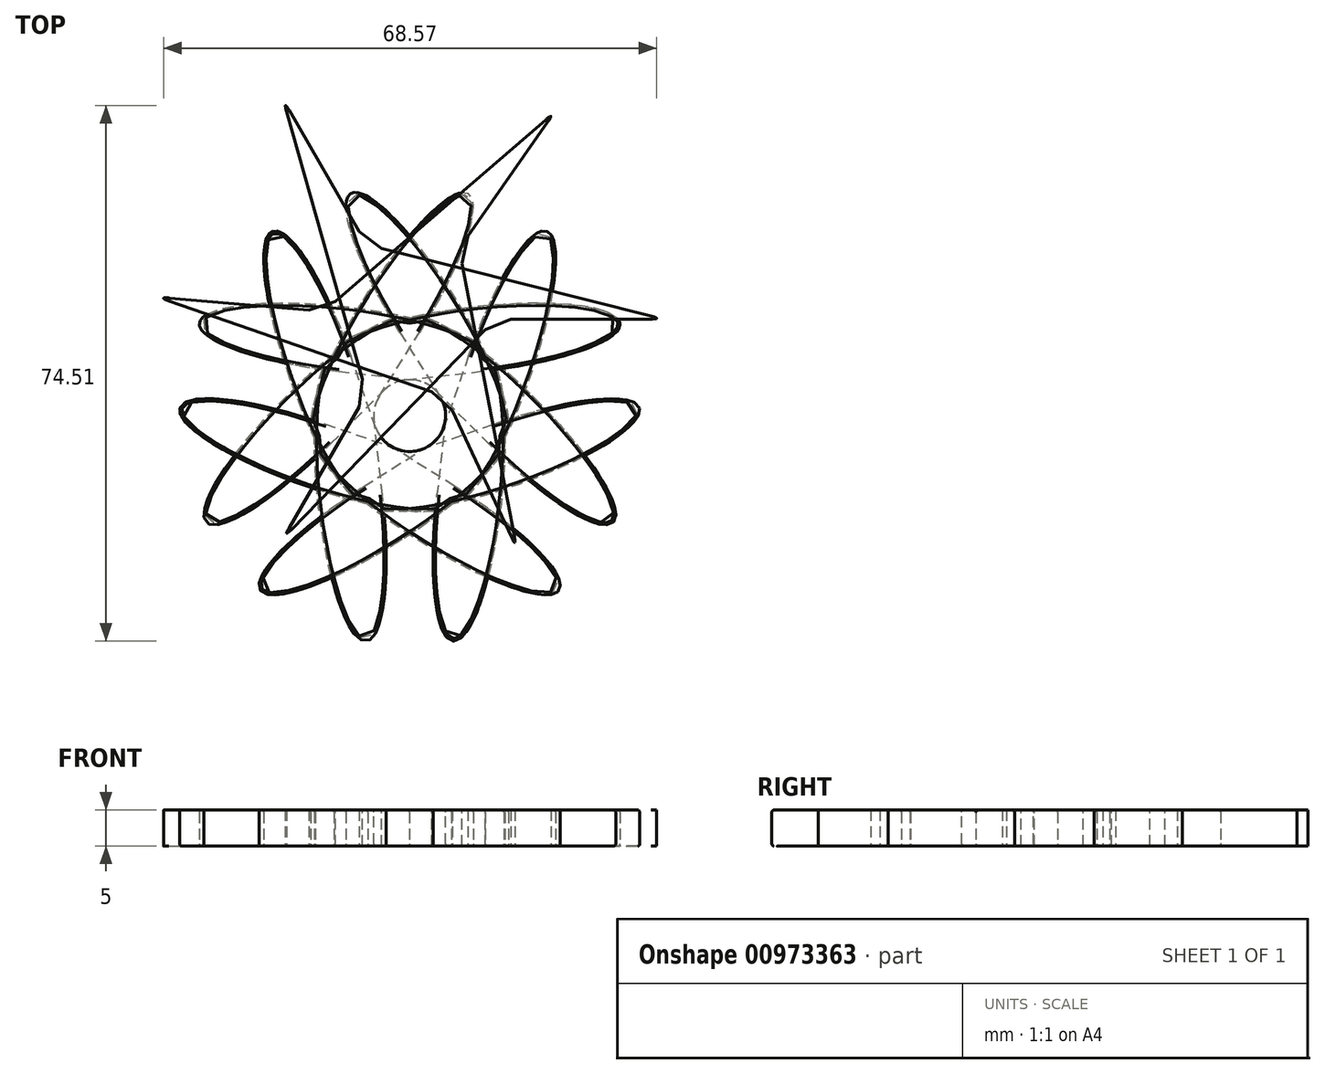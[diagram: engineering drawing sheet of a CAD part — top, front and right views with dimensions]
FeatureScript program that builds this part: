
annotation { "Feature Type Name" : "Feature", "Feature Type Description" : "" }
export const myFeature = defineFeature(function(context is Context, id is Id, definition is map)
    precondition{}
    {
        {
            var Q0;
            Q0=qCreatedBy(makeId("Top.planeOp"),FACE);
            var sketch = newSketch(context, id + "F0", { "sketchPlane" : qUnion([Q0])});
            skLineSegment(sketch, "E0", {"start": v(0, 0) * mm, "end": v(-2.73, 0) * mm});
            skLineSegment(sketch, "E1", {"start": v(0, 0) * mm, "end": v(0, -2.73) * mm});
            skLineSegment(sketch, "E2", {"start": v(0, 0) * mm, "end": v(-28.28, -28.28) * mm});
            skEllipticalArc(sketch, "E3", {});
            skLineSegment(sketch, "E4", {"start": v(0, -15.88) * mm, "end": v(0, 19.12) * mm});
            skEllipticalArc(sketch, "E5.MirrorC", {});
            skLineSegment(sketch, "E6.MirrorCS", {"start": v(0, 0) * mm, "end": v(28.28, -28.28) * mm});
            skLineSegment(sketch, "E7", {"start": v(-10.96, -17.32) * mm, "end": v(0, -6.36) * mm});
            skLineSegment(sketch, "E8", {"start": v(0, -6.36) * mm, "end": v(10.96, -17.32) * mm});
            const initialGuessF0  = {"E3": [-0.014142135623730956, -0.014142135623730956, 0.7071067811865476, 0.7071067811865476, 0.02, 0.0045, 0, 5.840556422484005], "E5.MirrorC": [0.014142135623730956, -0.014142135623730956, -0.7071067811865476, 0.7071067811865476, 0.02, 0.0045, 0.4426288846955803, 0]};
            skSetInitialGuess(sketch, initialGuessF0);
            skSolve(sketch);
        }
        {
            var Q0;
            {var subQ0=sQuery(id+"F0.wireOp",EDGE,"E1");var subQ1=makeQuery(id+"F0.imprint","IMPRINT",EDGE,{"derivedFrom":subQ0});var subQ2=sQuery(id+"F0.wireOp",EDGE,"E6.MirrorCS");var subQ3=makeQuery(id+"F0.imprint","IMPRINT",EDGE,{"derivedFrom":subQ2});var subQ8=sQuery(id+"F0.wireOp",EDGE,"E8");var subQ12=sQuery(id+"F0.wireOp",EDGE,"E7");var subQ19=sQuery(id+"F0.wireOp",EDGE,"E0");var subQ20=makeQuery(id+"F0.imprint","IMPRINT",EDGE,{"derivedFrom":subQ19});Q0=qUnion([makeQuery(id+"F0.imprint","IMPRINT",FACE,{"disambiguationData":[TD([[subQ20,-1.0]])]}),makeQuery(id+"F0.imprint","IMPRINT",FACE,{"disambiguationData":[TD([[subQ3,1.0]])]}),makeQuery(id+"F0.imprint","IMPRINT",FACE,{"disambiguationData":[TD([[subQ20,1.0]])]}),makeQuery(id+"F0.imprint","IMPRINT",FACE,{"disambiguationData":[TD([[makeQuery(id+"F0.imprint","IMPRINT",EDGE,{"derivedFrom":subQ12}),1.0]])]}),makeQuery(id+"F0.imprint","IMPRINT",FACE,{"disambiguationData":[TD([[makeQuery(id+"F0.imprint","IMPRINT",EDGE,{"derivedFrom":subQ8}),1.0]])]}),makeQuery(id+"F0.imprint","IMPRINT",FACE,{"disambiguationData":[TD([[subQ1,-1.0]])]}),makeQuery(id+"F0.imprint","IMPRINT",FACE,{"disambiguationData":[TD([[subQ1,1.0]])]})]);}
            extrude(context, id + "F1", {"entities" : qUnion([Q0]), "depth" : 5 * mm, "offsetDistance" : 25 * mm});
        }
        {
            var Q0;
            Q0=makeQuery(id+"F1.opExtrude","SWEPT_EDGE",EDGE,{"disambiguationData":[OSD([sQuery(id+"F0.wireOp",EDGE,"E4"),sQuery(id+"F0.wireOp",EDGE,"E7"),sQuery(id+"F0.wireOp",EDGE,"E8")])]});
            fillet(context, id + "F2", {"entities" : qUnion([Q0]), "tangentPropagation" : true, "radius" : 5 * mm, "defaultsChanged" : false, "vertexSettings" : [], "allowEdgeOverflow" : false});
        }
        {
            var Q0;
            Q0=makeQuery(id+"F1.opExtrude","CAP_FACE",FACE,{"disambiguationData":[OSD([sQuery(id+"F0.wireOp",EDGE,"E3"),sQuery(id+"F0.wireOp",EDGE,"E5.MirrorC"),sQuery(id+"F0.wireOp",EDGE,"E7"),sQuery(id+"F0.wireOp",EDGE,"E8")])],"isStart":false});
            var Q1;
            Q1=makeQuery(id+"F1.opExtrude","CAP_FACE",FACE,{"disambiguationData":[OSD([sQuery(id+"F0.wireOp",EDGE,"E3"),sQuery(id+"F0.wireOp",EDGE,"E5.MirrorC"),sQuery(id+"F0.wireOp",EDGE,"E7"),sQuery(id+"F0.wireOp",EDGE,"E8")])],"isStart":true});
            fillet(context, id + "F3", {"entities" : qUnion([Q0, Q1]), "tangentPropagation" : true, "radius" : 0.3 * mm, "defaultsChanged" : true, "vertexSettings" : [], "allowEdgeOverflow" : false});
        }
        {
            var Q0;
            Q0=makeQuery(id+"F1.opExtrude","SWEPT_BODY",BODY,{"disambiguationData":[OSD([sQuery(id+"F0.wireOp",EDGE,"E3"),sQuery(id+"F0.wireOp",EDGE,"E5.MirrorC"),sQuery(id+"F0.wireOp",EDGE,"E7"),sQuery(id+"F0.wireOp",EDGE,"E8")])]});
            var Q1;
            {var subQ0=sQuery(id+"F0.wireOp",EDGE,"E8");var subQ1=sQuery(id+"F0.wireOp",EDGE,"E7");var subQ2=makeQuery(id+"F1.opExtrude","CAP_FACE",FACE,{"disambiguationData":[OSD([sQuery(id+"F0.wireOp",EDGE,"E3"),sQuery(id+"F0.wireOp",EDGE,"E5.MirrorC"),subQ1,subQ0])],"isStart":true});Q1=makeQuery(id+"F3.opFillet","BLEND_EDGE",EDGE,{"blendedFrom":[makeQuery(id+"F2.opFillet","BLEND_EDGE",EDGE,{"blendedFrom":[makeQuery(id+"F1.opExtrude","SWEPT_EDGE",EDGE,{"disambiguationData":[OSD([sQuery(id+"F0.wireOp",EDGE,"E4"),subQ1,subQ0])]}),subQ2],"blendedInto":[subQ2]}),subQ2],"blendedInto":[subQ2]});}
            circularPattern(context, id + "F4", {"entities" : qUnion([Q0]), "axis" : qUnion([Q1]), "angle" : 360 * degree, "instanceCount" : 7, "equalSpace" : true});
        }
        {
            var Q0;
            Q0=qCreatedBy(makeId("Top.planeOp"),FACE);
            var sketch = newSketch(context, id + "F5", { "sketchPlane" : qUnion([Q0])});
            skLineSegment(sketch, "E9", {"start": v(0, 0) * mm, "end": v(0, 1) * mm});
            skLineSegment(sketch, "E10", {"start": v(35.14, 0) * mm, "end": v(0, 0) * mm});
            skLineSegment(sketch, "E11", {"start": v(0, 0) * mm, "end": v(7.07, 7.07) * mm});
            skLineSegment(sketch, "E12", {"start": v(7.07, 7.07) * mm, "end": v(35.14, 0) * mm});
            skCircle(sketch, "E13", {"center": v(0, 0) * mm, "radius": 1 * mm});
            skLineSegment(sketch, "E14.1.0", {"start": v(-9.66, 2.59) * mm, "end": v(-17.57, 30.43) * mm});
            skLineSegment(sketch, "E14.1.2", {"start": v(0, 0) * mm, "end": v(-9.66, 2.59) * mm});
            skLineSegment(sketch, "E14.2.0", {"start": v(2.59, -9.66) * mm, "end": v(-17.57, -30.43) * mm});
            skLineSegment(sketch, "E14.2.2", {"start": v(0, 0) * mm, "end": v(2.59, -9.66) * mm});
            skLineSegment(sketch, "E15", {"start": v(-17.57, 30.43) * mm, "end": v(0, 0) * mm});
            skLineSegment(sketch, "E16", {"start": v(-17.57, -30.43) * mm, "end": v(0, 0) * mm});
            skLineSegment(sketch, "E17", {"start": v(0, 0) * mm, "end": v(35.14, 0) * mm});
            skLineSegment(sketch, "E18", {"start": v(2.59, -9.66) * mm, "end": v(11.96, 0) * mm});
            skLineSegment(sketch, "E19.1.0", {"start": v(-9.66, 2.59) * mm, "end": v(-5.98, -10.36) * mm});
            skLineSegment(sketch, "E19.2.0", {"start": v(7.07, 7.07) * mm, "end": v(-5.98, 10.36) * mm});
            skLineSegment(sketch, "E19.anchor1", {"start": v(0, 0) * mm, "end": v(2.59, -9.66) * mm, "construction": true});
            skLineSegment(sketch, "E19.anchor2", {"start": v(0, 0) * mm, "end": v(7.07, 7.07) * mm, "construction": true});
            skSolve(sketch);
        }
        {
            var Q0;
            {var subQ3=sQuery(id+"F5.wireOp",EDGE,"E12");Q0=makeQuery(id+"F5.imprint","IMPRINT",FACE,{"disambiguationData":[TD([[makeQuery(id+"F5.imprint","IMPRINT",EDGE,{"derivedFrom":subQ3}),-1.0]])]});}
            var Q1;
            {var subQ0=sQuery(id+"F5.wireOp",EDGE,"E19.2.0");Q1=makeQuery(id+"F5.imprint","IMPRINT",FACE,{"disambiguationData":[TD([[makeQuery(id+"F5.imprint","IMPRINT",EDGE,{"derivedFrom":subQ0}),1.0]])]});}
            var Q2;
            {var subQ5=sQuery(id+"F5.wireOp",EDGE,"E19.1.0");Q2=makeQuery(id+"F5.imprint","IMPRINT",FACE,{"disambiguationData":[TD([[makeQuery(id+"F5.imprint","IMPRINT",EDGE,{"derivedFrom":subQ5}),1.0]])]});}
            var Q3;
            {var subQ1=sQuery(id+"F5.wireOp",EDGE,"E14.2.0");Q3=makeQuery(id+"F5.imprint","IMPRINT",FACE,{"disambiguationData":[TD([[makeQuery(id+"F5.imprint","IMPRINT",EDGE,{"derivedFrom":subQ1}),-1.0]])]});}
            var Q4;
            {var subQ0=sQuery(id+"F5.wireOp",EDGE,"E14.1.0");Q4=makeQuery(id+"F5.imprint","IMPRINT",FACE,{"disambiguationData":[TD([[makeQuery(id+"F5.imprint","IMPRINT",EDGE,{"derivedFrom":subQ0}),-1.0]])]});}
            var Q5;
            {var subQ0=sQuery(id+"F5.wireOp",EDGE,"E14.2.2");var subQ3=sQuery(id+"F5.wireOp",EDGE,"E13");var subQ5=makeQuery(id+"F5.imprint","INTERSECT",VERTEX,{"derivedFrom":[subQ3,subQ0]});Q5=makeQuery(id+"F5.imprint","IMPRINT",FACE,{"disambiguationData":[TD([[makeQuery(id+"F5.imprint","IMPRINT",EDGE,{"disambiguationData":[TD([[subQ5,-1.0]])],"derivedFrom":subQ3}),1.0]])]});}
            var Q6;
            {var subQ0=sQuery(id+"F5.wireOp",EDGE,"E11");var subQ3=sQuery(id+"F5.wireOp",EDGE,"E13");var subQ5=makeQuery(id+"F5.imprint","INTERSECT",VERTEX,{"derivedFrom":[subQ0,subQ3]});Q6=makeQuery(id+"F5.imprint","IMPRINT",FACE,{"disambiguationData":[TD([[makeQuery(id+"F5.imprint","IMPRINT",EDGE,{"disambiguationData":[TD([[subQ5,1.0]])],"derivedFrom":subQ3}),1.0]])]});}
            var Q7;
            {var subQ0=sQuery(id+"F5.wireOp",EDGE,"E9");Q7=makeQuery(id+"F5.imprint","IMPRINT",FACE,{"disambiguationData":[TD([[makeQuery(id+"F5.imprint","IMPRINT",EDGE,{"derivedFrom":subQ0}),-1.0]])]});}
            var Q8;
            {var subQ0=sQuery(id+"F5.wireOp",EDGE,"E9");Q8=makeQuery(id+"F5.imprint","IMPRINT",FACE,{"disambiguationData":[TD([[makeQuery(id+"F5.imprint","IMPRINT",EDGE,{"derivedFrom":subQ0}),1.0]])]});}
            var Q9;
            {var subQ0=sQuery(id+"F5.wireOp",EDGE,"E14.1.2");var subQ1=sQuery(id+"F5.wireOp",EDGE,"E13");var subQ2=makeQuery(id+"F5.imprint","INTERSECT",VERTEX,{"derivedFrom":[subQ1,subQ0]});Q9=makeQuery(id+"F5.imprint","IMPRINT",FACE,{"disambiguationData":[TD([[makeQuery(id+"F5.imprint","IMPRINT",EDGE,{"disambiguationData":[TD([[subQ2,1.0]])],"derivedFrom":subQ1}),1.0]])]});}
            var Q10;
            {var subQ0=sQuery(id+"F5.wireOp",EDGE,"E14.1.2");var subQ1=sQuery(id+"F5.wireOp",EDGE,"E13");var subQ2=makeQuery(id+"F5.imprint","INTERSECT",VERTEX,{"derivedFrom":[subQ1,subQ0]});Q10=makeQuery(id+"F5.imprint","IMPRINT",FACE,{"disambiguationData":[TD([[makeQuery(id+"F5.imprint","IMPRINT",EDGE,{"disambiguationData":[TD([[subQ2,-1.0]])],"derivedFrom":subQ1}),1.0]])]});}
            var Q11;
            {var subQ0=sQuery(id+"F5.wireOp",EDGE,"E14.2.2");var subQ1=sQuery(id+"F5.wireOp",EDGE,"E13");var subQ2=makeQuery(id+"F5.imprint","INTERSECT",VERTEX,{"derivedFrom":[subQ1,subQ0]});Q11=makeQuery(id+"F5.imprint","IMPRINT",FACE,{"disambiguationData":[TD([[makeQuery(id+"F5.imprint","IMPRINT",EDGE,{"disambiguationData":[TD([[subQ2,1.0]])],"derivedFrom":subQ1}),1.0]])]});}
            var Q12;
            {var subQ0=sQuery(id+"F5.wireOp",EDGE,"E18");Q12=makeQuery(id+"F5.imprint","IMPRINT",FACE,{"disambiguationData":[TD([[makeQuery(id+"F5.imprint","IMPRINT",EDGE,{"derivedFrom":subQ0}),1.0]])]});}
            extrude(context, id + "F6", {"entities" : qUnion([Q0, Q1, Q2, Q3, Q4, Q5, Q6, Q7, Q8, Q9, Q10, Q11, Q12]), "depth" : 5 * mm, "offsetDistance" : 25 * mm});
        }
        {
            var Q0;
            Q0=makeQuery(id+"F6.opExtrude","SWEPT_EDGE",EDGE,{"disambiguationData":[OSD([sQuery(id+"F5.wireOp",EDGE,"E10"),sQuery(id+"F5.wireOp",EDGE,"E18")])]});
            var Q1;
            Q1=makeQuery(id+"F6.opExtrude","SWEPT_EDGE",EDGE,{"disambiguationData":[OSD([sQuery(id+"F5.wireOp",EDGE,"E16"),sQuery(id+"F5.wireOp",EDGE,"E19.1.0")])]});
            var Q2;
            Q2=makeQuery(id+"F6.opExtrude","SWEPT_EDGE",EDGE,{"disambiguationData":[OSD([sQuery(id+"F5.wireOp",EDGE,"E15"),sQuery(id+"F5.wireOp",EDGE,"E19.2.0")])]});
            chamfer(context, id + "F7", {"entities" : qUnion([Q0, Q1, Q2]), "width" : 5 * mm, "tangentPropagation" : true});
        }
        {
            var Q0;
            Q0=makeQuery(id+"F6.opExtrude","SWEPT_EDGE",EDGE,{"disambiguationData":[OSD([sQuery(id+"F5.wireOp",EDGE,"E14.2.0"),sQuery(id+"F5.wireOp",EDGE,"E16")])]});
            var Q1;
            Q1=makeQuery(id+"F6.opExtrude","SWEPT_EDGE",EDGE,{"disambiguationData":[OSD([sQuery(id+"F5.wireOp",EDGE,"E14.1.0"),sQuery(id+"F5.wireOp",EDGE,"E15")])]});
            var Q2;
            Q2=makeQuery(id+"F6.opExtrude","SWEPT_EDGE",EDGE,{"disambiguationData":[OSD([sQuery(id+"F5.wireOp",EDGE,"E10"),sQuery(id+"F5.wireOp",EDGE,"E12")])]});
            fillet(context, id + "F8", {"entities" : qUnion([Q0, Q1, Q2]), "tangentPropagation" : true, "crossSection" : FilletCrossSection.CONIC, "radius" : 0.2 * mm, "rho" : 0.5, "defaultsChanged" : false, "vertexSettings" : [], "allowEdgeOverflow" : false});
        }
        {
            var Q0;
            Q0=makeQuery(id+"F6.opExtrude","CAP_FACE",FACE,{"disambiguationData":[OSD([sQuery(id+"F5.wireOp",EDGE,"E10"),sQuery(id+"F5.wireOp",EDGE,"E12"),sQuery(id+"F5.wireOp",EDGE,"E14.1.0"),sQuery(id+"F5.wireOp",EDGE,"E14.2.0"),sQuery(id+"F5.wireOp",EDGE,"E15"),sQuery(id+"F5.wireOp",EDGE,"E16"),sQuery(id+"F5.wireOp",EDGE,"E18"),sQuery(id+"F5.wireOp",EDGE,"E19.1.0"),sQuery(id+"F5.wireOp",EDGE,"E19.2.0")])],"isStart":true});
            var sketch = newSketch(context, id + "F9", { "sketchPlane" : qUnion([Q0])});
            skCircle(sketch, "E20", {"center": v(0, 0) * mm, "radius": 6.6 * mm});
            skSolve(sketch);
        }
        {
            var Q0;
            Q0=makeQuery(id+"F6.opExtrude","SWEPT_BODY",BODY,{"disambiguationData":[OSD([sQuery(id+"F5.wireOp",EDGE,"E10"),sQuery(id+"F5.wireOp",EDGE,"E12"),sQuery(id+"F5.wireOp",EDGE,"E14.1.0"),sQuery(id+"F5.wireOp",EDGE,"E14.2.0"),sQuery(id+"F5.wireOp",EDGE,"E15"),sQuery(id+"F5.wireOp",EDGE,"E16"),sQuery(id+"F5.wireOp",EDGE,"E18"),sQuery(id+"F5.wireOp",EDGE,"E19.1.0"),sQuery(id+"F5.wireOp",EDGE,"E19.2.0")])]});
            var Q1;
            Q1=sQuery(id+"F9.wireOp",EDGE,"E20");
            transform(context, id + "F10", {"entities" : qUnion([Q0]), "transformType" : TransformType.ROTATION, "transformAxis" : qUnion([Q1]), "angle" : 55 * degree, "oppositeDirection" : true, "makeCopy" : true});
        }
    });
